# Revit family: Haworth_Zody_Stool_Task
name_source: partatom
category: Furniture
revit_build: Autodesk Revit 2018 (Build: 20170223_1515(x64)
units: mm (PartAtom-declared; Revit-internal decimal feet)

## family parameters
Always vertical = Yes
Cut with Voids When Loaded = No
OmniClass Number = 23.40.70.14.64.11
OmniClass Title = Office Furniture
Room Calculation Point = No
Shared = No
Work Plane-Based = No

## types (6) — shared parameters
Assembly Code = E2020200
Caster Finish = Haworth _ Polymer _ Black
Depth = 29 "
Description = Haworth Zody Stool Task
Footring Finish = Haworth _ Metal _ Brushed Aluminum
Hardware Finish = Haworth _ Paint _ Black
Lumbar Finish = Haworth _ Polymer _ Slate
Manufacturer = Haworth
Model = SZTC-20
Revision Number = 2
Support Finish = Haworth _ Metal _ Stainless Steel
Sustainability Info = http://media.haworth.com
URL = http://www.haworth.com
URL - Product = https://www.haworth.com
Warranty = http://www.haworth.com
Width = 29 "

## per-type parameters (varying)
| type | Arms | Fixed Arms | Height Adjustable Arms | With Lumbar | Without Arms | Without Lumbar |
| SZTC-20-41 - Height Adjustable Arms - With Lumbar | Yes | No | Yes | Yes | No | No |
| SZTC-20-01 - Without Arms - With Lumbar | No | No | No | Yes | Yes | No |
| SZTC-20-11 - Fixed Arms - With Lumbar | Yes | Yes | No | Yes | No | No |
| SZTC-20-40 - Height Adjustable Arms - Without Lumbar | Yes | No | Yes | No | No | Yes |
| SZTC-20-00 - Without Arms - Without Lumbar | No | No | No | No | Yes | Yes |
| SZTC-20-10 - Fixed Arms - Without Lumbar | Yes | Yes | No | No | No | Yes |

## geometry (parser evidence)
native form markers: Blend x9, Sweep x10
no freeform markers — native parametric forms only
